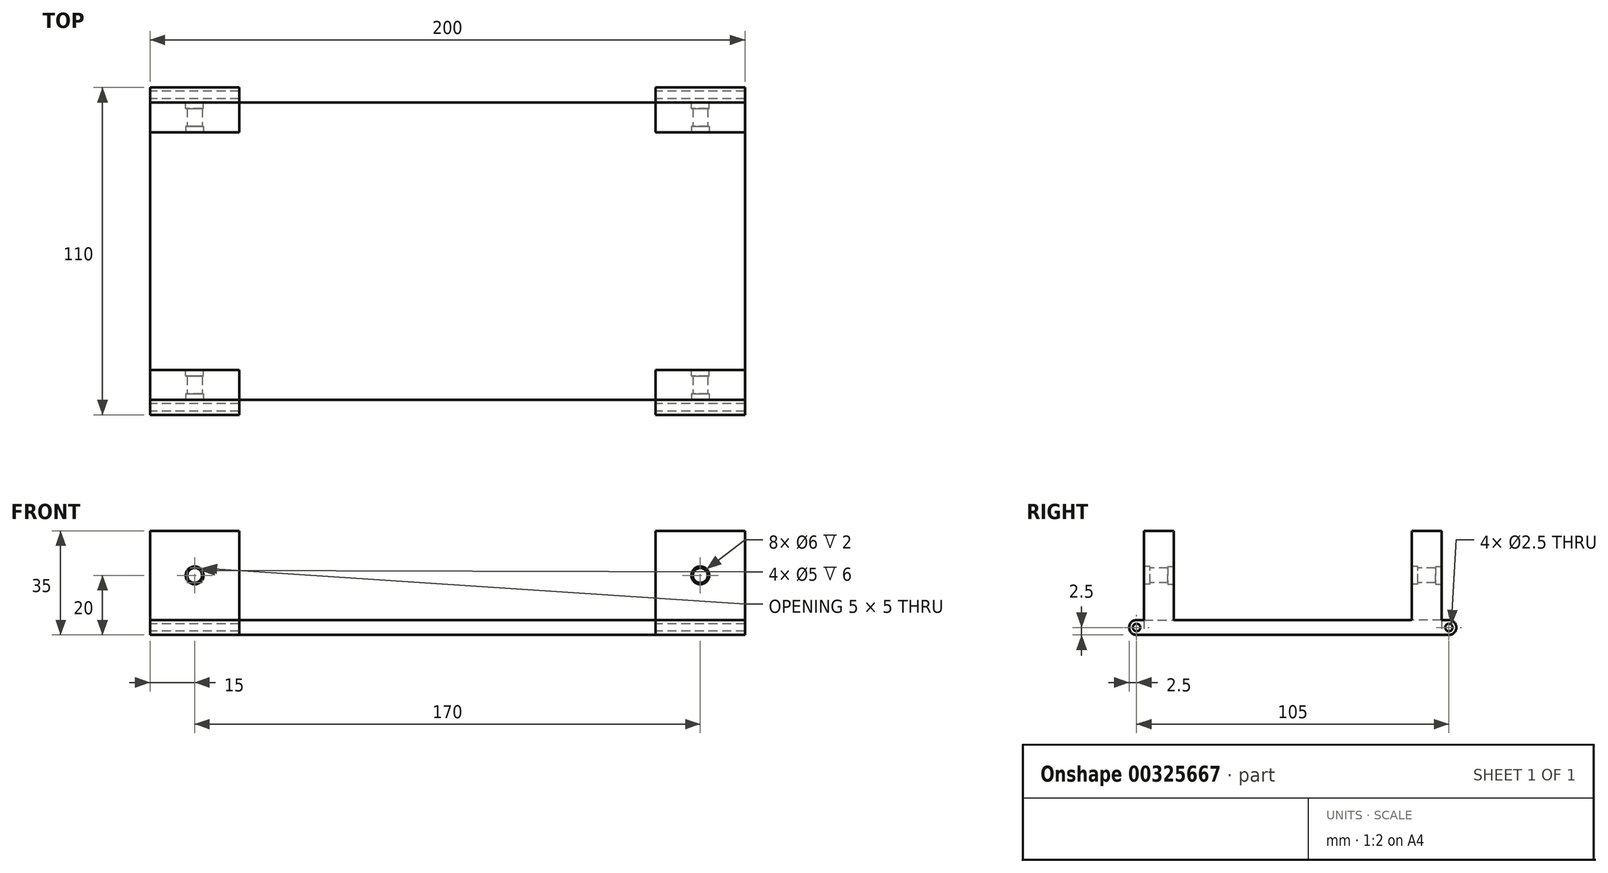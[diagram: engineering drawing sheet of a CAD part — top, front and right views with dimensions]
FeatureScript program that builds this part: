
annotation { "Feature Type Name" : "Feature", "Feature Type Description" : "" }
export const myFeature = defineFeature(function(context is Context, id is Id, definition is map)
    precondition{}
    {
        {
            var Q0;
            Q0=qCreatedBy(makeId("Top.planeOp"),FACE);
            var sketch = newSketch(context, id + "F0", { "sketchPlane" : qUnion([Q0])});
            skLineSegment(sketch, "E0.bottom", {"start": v(103.79, -50) * mm, "end": v(-96.21, -50) * mm});
            skLineSegment(sketch, "E0.top", {"start": v(103.79, 50) * mm, "end": v(-96.21, 50) * mm});
            skLineSegment(sketch, "E0.left", {"start": v(103.79, -50) * mm, "end": v(103.79, 50) * mm});
            skLineSegment(sketch, "E0.right", {"start": v(-96.21, -50) * mm, "end": v(-96.21, 50) * mm});
            skPoint(sketch, "E0.middle", {"position": v(3.79, 0) * mm});
            skSolve(sketch);
        }
        {
            var Q0;
            Q0=makeQuery(id+"F0.imprint","IMPRINT",FACE,{"disambiguationData":[TD([[makeQuery(id+"F0.imprint","IMPRINT",EDGE,{"derivedFrom":sQuery(id+"F0.wireOp",EDGE,"E0.bottom")}),-1.0]])]});
            extrude(context, id + "F1", {"entities" : qUnion([Q0]), "depth" : 5 * mm});
        }
        {
            var Q0;
            Q0=makeQuery(id+"F1.opExtrude","CAP_FACE",FACE,{"disambiguationData":[OSD([sQuery(id+"F0.wireOp",EDGE,"E0.bottom"),sQuery(id+"F0.wireOp",EDGE,"E0.top"),sQuery(id+"F0.wireOp",EDGE,"E0.left"),sQuery(id+"F0.wireOp",EDGE,"E0.right")])],"isStart":false});
            var sketch = newSketch(context, id + "F2", { "sketchPlane" : qUnion([Q0])});
            skLineSegment(sketch, "E1.bottom", {"start": v(103.79, -50) * mm, "end": v(73.79, -50) * mm});
            skLineSegment(sketch, "E1.top", {"start": v(103.79, -40) * mm, "end": v(73.79, -40) * mm});
            skLineSegment(sketch, "E1.left", {"start": v(103.79, -50) * mm, "end": v(103.79, -40) * mm});
            skLineSegment(sketch, "E1.right", {"start": v(73.79, -50) * mm, "end": v(73.79, -40) * mm});
            skLineSegment(sketch, "E2.bottom", {"start": v(103.79, 50) * mm, "end": v(73.79, 50) * mm});
            skLineSegment(sketch, "E2.top", {"start": v(103.79, 40) * mm, "end": v(73.79, 40) * mm});
            skLineSegment(sketch, "E2.left", {"start": v(103.79, 50) * mm, "end": v(103.79, 40) * mm});
            skLineSegment(sketch, "E2.right", {"start": v(73.79, 50) * mm, "end": v(73.79, 40) * mm});
            skLineSegment(sketch, "E3.bottom", {"start": v(-96.21, 50) * mm, "end": v(-66.21, 50) * mm});
            skLineSegment(sketch, "E3.top", {"start": v(-96.21, 40) * mm, "end": v(-66.21, 40) * mm});
            skLineSegment(sketch, "E3.left", {"start": v(-96.21, 50) * mm, "end": v(-96.21, 40) * mm});
            skLineSegment(sketch, "E3.right", {"start": v(-66.21, 50) * mm, "end": v(-66.21, 40) * mm});
            skLineSegment(sketch, "E4.bottom", {"start": v(-96.21, -50) * mm, "end": v(-66.21, -50) * mm});
            skLineSegment(sketch, "E4.top", {"start": v(-96.21, -40) * mm, "end": v(-66.21, -40) * mm});
            skLineSegment(sketch, "E4.left", {"start": v(-96.21, -50) * mm, "end": v(-96.21, -40) * mm});
            skLineSegment(sketch, "E4.right", {"start": v(-66.21, -50) * mm, "end": v(-66.21, -40) * mm});
            skSolve(sketch);
        }
        {
            var Q0;
            Q0=makeQuery(id+"F2.imprint","IMPRINT",FACE,{"disambiguationData":[TD([[makeQuery(id+"F2.imprint","IMPRINT",EDGE,{"derivedFrom":sQuery(id+"F2.wireOp",EDGE,"E3.bottom")}),1.0]])]});
            var Q1;
            Q1=makeQuery(id+"F2.imprint","IMPRINT",FACE,{"disambiguationData":[TD([[makeQuery(id+"F2.imprint","IMPRINT",EDGE,{"derivedFrom":sQuery(id+"F2.wireOp",EDGE,"E2.bottom")}),1.0]])]});
            var Q2;
            Q2=makeQuery(id+"F2.imprint","IMPRINT",FACE,{"disambiguationData":[TD([[makeQuery(id+"F2.imprint","IMPRINT",EDGE,{"derivedFrom":sQuery(id+"F2.wireOp",EDGE,"E4.bottom")}),-1.0]])]});
            var Q3;
            Q3=makeQuery(id+"F2.imprint","IMPRINT",FACE,{"disambiguationData":[TD([[makeQuery(id+"F2.imprint","IMPRINT",EDGE,{"derivedFrom":sQuery(id+"F2.wireOp",EDGE,"E1.bottom")}),-1.0]])]});
            extrude(context, id + "F3", {"entities" : qUnion([Q0, Q1, Q2, Q3]), "operationType" : NewBodyOperationType.ADD, "depth" : 30 * mm});
        }
        {
            var Q0;
            Q0=makeQuery(id+"F3.boolean.opBoolean","MERGE",FACE,{"derivedFrom":[makeQuery(id+"F1.opExtrude","SWEPT_FACE",FACE,{"disambiguationData":[OSD([sQuery(id+"F0.wireOp",EDGE,"E0.bottom")])]}),makeQuery(id+"F3.opExtrude","SWEPT_FACE",FACE,{"disambiguationData":[OSD([sQuery(id+"F2.wireOp",EDGE,"E1.bottom")])]}),makeQuery(id+"F3.opExtrude","SWEPT_FACE",FACE,{"disambiguationData":[OSD([sQuery(id+"F2.wireOp",EDGE,"E4.bottom")])]})]});
            var sketch = newSketch(context, id + "F4", { "sketchPlane" : qUnion([Q0])});
            skCircle(sketch, "E5", {"center": v(88.79, 20) * mm, "radius": 2.5 * mm});
            skCircle(sketch, "E6", {"center": v(-81.21, 20) * mm, "radius": 2.5 * mm});
            skSolve(sketch);
        }
        {
            var Q0;
            Q0=makeQuery(id+"F4.imprint","IMPRINT",FACE,{"disambiguationData":[TD([[makeQuery(id+"F4.imprint","IMPRINT",EDGE,{"derivedFrom":sQuery(id+"F4.wireOp",EDGE,"E5")}),1.0]])]});
            var Q1;
            Q1=makeQuery(id+"F4.imprint","IMPRINT",FACE,{"disambiguationData":[TD([[makeQuery(id+"F4.imprint","IMPRINT",EDGE,{"derivedFrom":sQuery(id+"F4.wireOp",EDGE,"E6")}),1.0]])]});
            extrude(context, id + "F5", {"entities" : qUnion([Q0, Q1]), "operationType" : NewBodyOperationType.REMOVE, "endBound" : BoundingType.THROUGH_ALL, "oppositeDirection" : true, "depth" : 25 * mm});
        }
        {
            var Q0;
            Q0=makeQuery(id+"F3.boolean.opBoolean","MERGE",FACE,{"derivedFrom":[makeQuery(id+"F1.opExtrude","SWEPT_FACE",FACE,{"disambiguationData":[OSD([sQuery(id+"F0.wireOp",EDGE,"E0.bottom")])]}),makeQuery(id+"F3.opExtrude","SWEPT_FACE",FACE,{"disambiguationData":[OSD([sQuery(id+"F2.wireOp",EDGE,"E1.bottom")])]}),makeQuery(id+"F3.opExtrude","SWEPT_FACE",FACE,{"disambiguationData":[OSD([sQuery(id+"F2.wireOp",EDGE,"E4.bottom")])]})]});
            var sketch = newSketch(context, id + "F6", { "sketchPlane" : qUnion([Q0])});
            skCircle(sketch, "E7", {"center": v(-81.21, 20) * mm, "radius": 3 * mm});
            skCircle(sketch, "E8", {"center": v(88.79, 20) * mm, "radius": 3 * mm});
            skSolve(sketch);
        }
        {
            var Q0;
            Q0=makeQuery(id+"F6.imprint","IMPRINT",FACE,{"disambiguationData":[TD([[makeQuery(id+"F6.imprint","IMPRINT",EDGE,{"derivedFrom":sQuery(id+"F6.wireOp",EDGE,"E8")}),1.0]])]});
            var Q1;
            Q1=makeQuery(id+"F6.imprint","IMPRINT",FACE,{"disambiguationData":[TD([[makeQuery(id+"F6.imprint","IMPRINT",EDGE,{"derivedFrom":sQuery(id+"F6.wireOp",EDGE,"E7")}),1.0]])]});
            extrude(context, id + "F7", {"entities" : qUnion([Q0, Q1]), "operationType" : NewBodyOperationType.REMOVE, "oppositeDirection" : true, "depth" : 2 * mm, "hasSecondDirection" : true, "secondDirectionOppositeDirection" : false, "secondDirectionDepth" : 25 * mm});
        }
        {
            var Q0;
            Q0=makeQuery(id+"F3.opExtrude","SWEPT_FACE",FACE,{"disambiguationData":[OSD([sQuery(id+"F2.wireOp",EDGE,"E3.top")])]});
            var sketch = newSketch(context, id + "F8", { "sketchPlane" : qUnion([Q0])});
            skCircle(sketch, "E9", {"center": v(-81.21, 20) * mm, "radius": 3 * mm});
            skCircle(sketch, "E10", {"center": v(88.79, 20) * mm, "radius": 3 * mm});
            skSolve(sketch);
        }
        {
            var Q0;
            Q0=makeQuery(id+"F8.imprint","IMPRINT",FACE,{"disambiguationData":[TD([[makeQuery(id+"F8.imprint","IMPRINT",EDGE,{"derivedFrom":sQuery(id+"F8.wireOp",EDGE,"E9")}),1.0]])]});
            extrude(context, id + "F9", {"entities" : qUnion([Q0]), "operationType" : NewBodyOperationType.REMOVE, "oppositeDirection" : true, "depth" : 2 * mm});
        }
        {
            var Q0;
            Q0=makeQuery(id+"F3.opExtrude","SWEPT_FACE",FACE,{"disambiguationData":[OSD([sQuery(id+"F2.wireOp",EDGE,"E2.top")])]});
            var sketch = newSketch(context, id + "F10", { "sketchPlane" : qUnion([Q0])});
            skCircle(sketch, "E11", {"center": v(88.79, 20) * mm, "radius": 3 * mm});
            skSolve(sketch);
        }
        {
            var Q0;
            Q0=makeQuery(id+"F10.imprint","IMPRINT",FACE,{"disambiguationData":[TD([[makeQuery(id+"F10.imprint","IMPRINT",EDGE,{"derivedFrom":sQuery(id+"F10.wireOp",EDGE,"E11")}),1.0]])]});
            extrude(context, id + "F11", {"entities" : qUnion([Q0]), "operationType" : NewBodyOperationType.REMOVE, "oppositeDirection" : true, "depth" : 2 * mm});
        }
        {
            var Q0;
            Q0=makeQuery(id+"F3.boolean.opBoolean","MERGE",FACE,{"derivedFrom":[makeQuery(id+"F1.opExtrude","SWEPT_FACE",FACE,{"disambiguationData":[OSD([sQuery(id+"F0.wireOp",EDGE,"E0.top")])]}),makeQuery(id+"F3.opExtrude","SWEPT_FACE",FACE,{"disambiguationData":[OSD([sQuery(id+"F2.wireOp",EDGE,"E2.bottom")])]}),makeQuery(id+"F3.opExtrude","SWEPT_FACE",FACE,{"disambiguationData":[OSD([sQuery(id+"F2.wireOp",EDGE,"E3.bottom")])]})]});
            var sketch = newSketch(context, id + "F12", { "sketchPlane" : qUnion([Q0])});
            skCircle(sketch, "E12", {"center": v(-88.79, 20) * mm, "radius": 3 * mm});
            skCircle(sketch, "E13", {"center": v(81.21, 20) * mm, "radius": 3 * mm});
            skSolve(sketch);
        }
        {
            var Q0;
            Q0=makeQuery(id+"F12.imprint","IMPRINT",FACE,{"disambiguationData":[TD([[makeQuery(id+"F12.imprint","IMPRINT",EDGE,{"derivedFrom":sQuery(id+"F12.wireOp",EDGE,"E13")}),1.0]])]});
            var Q1;
            Q1=makeQuery(id+"F12.imprint","IMPRINT",FACE,{"disambiguationData":[TD([[makeQuery(id+"F12.imprint","IMPRINT",EDGE,{"derivedFrom":sQuery(id+"F12.wireOp",EDGE,"E12")}),1.0]])]});
            extrude(context, id + "F13", {"entities" : qUnion([Q0, Q1]), "operationType" : NewBodyOperationType.REMOVE, "oppositeDirection" : true, "depth" : 2 * mm});
        }
        {
            var Q0;
            Q0=makeQuery(id+"F3.opExtrude","SWEPT_FACE",FACE,{"disambiguationData":[OSD([sQuery(id+"F2.wireOp",EDGE,"E4.top")])]});
            var sketch = newSketch(context, id + "F14", { "sketchPlane" : qUnion([Q0])});
            skCircle(sketch, "E14", {"center": v(81.21, 20) * mm, "radius": 3 * mm});
            skCircle(sketch, "E15", {"center": v(-88.79, 20) * mm, "radius": 3 * mm});
            skSolve(sketch);
        }
        {
            var Q0;
            Q0=makeQuery(id+"F14.imprint","IMPRINT",FACE,{"disambiguationData":[TD([[makeQuery(id+"F14.imprint","IMPRINT",EDGE,{"derivedFrom":makeQuery(id+"F5.boolean.opBoolean","INTERSECT",EDGE,{"derivedFrom":[makeQuery(id+"F3.opExtrude","SWEPT_FACE",FACE,{"disambiguationData":[OSD([sQuery(id+"F2.wireOp",EDGE,"E4.top")])]}),makeQuery(id+"F5.opExtrude","SWEPT_FACE",FACE,{"disambiguationData":[OSD([sQuery(id+"F4.wireOp",EDGE,"E6")])]})]})}),1.0]])]});
            var Q1;
            Q1=makeQuery(id+"F14.imprint","IMPRINT",FACE,{"disambiguationData":[TD([[makeQuery(id+"F14.imprint","IMPRINT",EDGE,{"derivedFrom":sQuery(id+"F14.wireOp",EDGE,"E14")}),1.0]])]});
            extrude(context, id + "F15", {"entities" : qUnion([Q0, Q1]), "operationType" : NewBodyOperationType.REMOVE, "oppositeDirection" : true, "depth" : 2 * mm});
        }
        {
            var Q0;
            Q0=makeQuery(id+"F3.opExtrude","SWEPT_FACE",FACE,{"disambiguationData":[OSD([sQuery(id+"F2.wireOp",EDGE,"E1.top")])]});
            var sketch = newSketch(context, id + "F16", { "sketchPlane" : qUnion([Q0])});
            skCircle(sketch, "E16", {"center": v(-88.79, 20) * mm, "radius": 3 * mm});
            skSolve(sketch);
        }
        {
            var Q0;
            Q0=makeQuery(id+"F16.imprint","IMPRINT",FACE,{"disambiguationData":[TD([[makeQuery(id+"F16.imprint","IMPRINT",EDGE,{"derivedFrom":sQuery(id+"F16.wireOp",EDGE,"E16")}),1.0]])]});
            extrude(context, id + "F17", {"entities" : qUnion([Q0]), "operationType" : NewBodyOperationType.REMOVE, "oppositeDirection" : true, "depth" : 2 * mm});
        }
        {
            var Q0;
            Q0=makeQuery(id+"F3.boolean.opBoolean","MERGE",FACE,{"derivedFrom":[makeQuery(id+"F1.opExtrude","SWEPT_FACE",FACE,{"disambiguationData":[OSD([sQuery(id+"F0.wireOp",EDGE,"E0.bottom")])]}),makeQuery(id+"F3.opExtrude","SWEPT_FACE",FACE,{"disambiguationData":[OSD([sQuery(id+"F2.wireOp",EDGE,"E1.bottom")])]}),makeQuery(id+"F3.opExtrude","SWEPT_FACE",FACE,{"disambiguationData":[OSD([sQuery(id+"F2.wireOp",EDGE,"E4.bottom")])]})]});
            var sketch = newSketch(context, id + "F18", { "sketchPlane" : qUnion([Q0])});
            skLineSegment(sketch, "E17.bottom", {"start": v(-96.21, 0) * mm, "end": v(-66.21, 0) * mm});
            skLineSegment(sketch, "E17.top", {"start": v(-96.21, 5) * mm, "end": v(-66.21, 5) * mm});
            skLineSegment(sketch, "E17.left", {"start": v(-96.21, 0) * mm, "end": v(-96.21, 5) * mm});
            skLineSegment(sketch, "E17.right", {"start": v(-66.21, 0) * mm, "end": v(-66.21, 5) * mm});
            skLineSegment(sketch, "E18.bottom", {"start": v(73.79, 5) * mm, "end": v(103.79, 5) * mm});
            skLineSegment(sketch, "E18.top", {"start": v(73.79, 0) * mm, "end": v(103.79, 0) * mm});
            skLineSegment(sketch, "E18.left", {"start": v(73.79, 5) * mm, "end": v(73.79, 0) * mm});
            skLineSegment(sketch, "E18.right", {"start": v(103.79, 5) * mm, "end": v(103.79, 0) * mm});
            skSolve(sketch);
        }
        {
            var Q0;
            Q0=makeQuery(id+"F18.imprint","IMPRINT",FACE,{"disambiguationData":[TD([[makeQuery(id+"F18.imprint","IMPRINT",EDGE,{"derivedFrom":sQuery(id+"F18.wireOp",EDGE,"E17.bottom")}),-1.0]])]});
            var Q1;
            Q1=makeQuery(id+"F18.imprint","IMPRINT",FACE,{"disambiguationData":[TD([[makeQuery(id+"F18.imprint","IMPRINT",EDGE,{"derivedFrom":sQuery(id+"F18.wireOp",EDGE,"E18.bottom")}),-1.0]])]});
            extrude(context, id + "F19", {"entities" : qUnion([Q0, Q1]), "operationType" : NewBodyOperationType.ADD, "depth" : 5 * mm});
        }
        {
            var Q0;
            Q0=makeQuery(id+"F19.boolean.opBoolean","MERGE",FACE,{"derivedFrom":[makeQuery(id+"F3.boolean.opBoolean","MERGE",FACE,{"derivedFrom":[makeQuery(id+"F1.opExtrude","SWEPT_FACE",FACE,{"disambiguationData":[OSD([sQuery(id+"F0.wireOp",EDGE,"E0.right")])]}),makeQuery(id+"F3.opExtrude","SWEPT_FACE",FACE,{"disambiguationData":[OSD([sQuery(id+"F2.wireOp",EDGE,"E3.left")])]}),makeQuery(id+"F3.opExtrude","SWEPT_FACE",FACE,{"disambiguationData":[OSD([sQuery(id+"F2.wireOp",EDGE,"E4.left")])]})]}),makeQuery(id+"F19.opExtrude","SWEPT_FACE",FACE,{"disambiguationData":[OSD([sQuery(id+"F18.wireOp",EDGE,"E17.left")])]})]});
            var sketch = newSketch(context, id + "F20", { "sketchPlane" : qUnion([Q0])});
            skCircle(sketch, "E19", {"center": v(52.5, 2.5) * mm, "radius": 1.25 * mm});
            skSolve(sketch);
        }
        {
            var Q0;
            Q0=makeQuery(id+"F20.imprint","IMPRINT",FACE,{"disambiguationData":[TD([[makeQuery(id+"F20.imprint","IMPRINT",EDGE,{"derivedFrom":sQuery(id+"F20.wireOp",EDGE,"E19")}),1.0]])]});
            extrude(context, id + "F21", {"entities" : qUnion([Q0]), "operationType" : NewBodyOperationType.REMOVE, "endBound" : BoundingType.THROUGH_ALL, "oppositeDirection" : true, "depth" : 25 * mm});
        }
        {
            var Q0;
            Q0=makeQuery(id+"F19.opExtrude","CAP_EDGE",EDGE,{"disambiguationData":[OSD([sQuery(id+"F18.wireOp",EDGE,"E17.top")])],"isStart":false});
            var Q1;
            Q1=makeQuery(id+"F19.opExtrude","CAP_EDGE",EDGE,{"disambiguationData":[OSD([sQuery(id+"F18.wireOp",EDGE,"E17.bottom")])],"isStart":false});
            var Q2;
            Q2=makeQuery(id+"F19.opExtrude","CAP_EDGE",EDGE,{"disambiguationData":[OSD([sQuery(id+"F18.wireOp",EDGE,"E18.bottom")])],"isStart":false});
            var Q3;
            Q3=makeQuery(id+"F19.opExtrude","CAP_EDGE",EDGE,{"disambiguationData":[OSD([sQuery(id+"F18.wireOp",EDGE,"E18.top")])],"isStart":false});
            fillet(context, id + "F22", {"entities" : qUnion([Q0, Q1, Q2, Q3]), "radius" : 2.5 * mm, "tangentPropagation" : true, "allowEdgeOverflow" : false});
        }
        {
            var Q0;
            Q0=makeQuery(id+"F3.boolean.opBoolean","MERGE",FACE,{"derivedFrom":[makeQuery(id+"F1.opExtrude","SWEPT_FACE",FACE,{"disambiguationData":[OSD([sQuery(id+"F0.wireOp",EDGE,"E0.top")])]}),makeQuery(id+"F3.opExtrude","SWEPT_FACE",FACE,{"disambiguationData":[OSD([sQuery(id+"F2.wireOp",EDGE,"E2.bottom")])]}),makeQuery(id+"F3.opExtrude","SWEPT_FACE",FACE,{"disambiguationData":[OSD([sQuery(id+"F2.wireOp",EDGE,"E3.bottom")])]})]});
            var sketch = newSketch(context, id + "F23", { "sketchPlane" : qUnion([Q0])});
            skLineSegment(sketch, "E20.bottom", {"start": v(66.21, 5) * mm, "end": v(96.21, 5) * mm});
            skLineSegment(sketch, "E20.top", {"start": v(66.21, 0) * mm, "end": v(96.21, 0) * mm});
            skLineSegment(sketch, "E20.left", {"start": v(66.21, 5) * mm, "end": v(66.21, 0) * mm});
            skLineSegment(sketch, "E20.right", {"start": v(96.21, 5) * mm, "end": v(96.21, 0) * mm});
            skLineSegment(sketch, "E21.bottom", {"start": v(-73.79, 5) * mm, "end": v(-103.79, 5) * mm});
            skLineSegment(sketch, "E21.top", {"start": v(-73.79, 0) * mm, "end": v(-103.79, 0) * mm});
            skLineSegment(sketch, "E21.left", {"start": v(-73.79, 5) * mm, "end": v(-73.79, 0) * mm});
            skLineSegment(sketch, "E21.right", {"start": v(-103.79, 5) * mm, "end": v(-103.79, 0) * mm});
            skSolve(sketch);
        }
        {
            var Q0;
            Q0=makeQuery(id+"F23.imprint","IMPRINT",FACE,{"disambiguationData":[TD([[makeQuery(id+"F23.imprint","IMPRINT",EDGE,{"derivedFrom":sQuery(id+"F23.wireOp",EDGE,"E21.bottom")}),1.0]])]});
            var Q1;
            Q1=makeQuery(id+"F23.imprint","IMPRINT",FACE,{"disambiguationData":[TD([[makeQuery(id+"F23.imprint","IMPRINT",EDGE,{"derivedFrom":sQuery(id+"F23.wireOp",EDGE,"E20.bottom")}),-1.0]])]});
            extrude(context, id + "F24", {"entities" : qUnion([Q0, Q1]), "operationType" : NewBodyOperationType.ADD, "depth" : 5 * mm});
        }
        {
            var Q0;
            Q0=makeQuery(id+"F24.boolean.opBoolean","MERGE",FACE,{"derivedFrom":[makeQuery(id+"F19.boolean.opBoolean","MERGE",FACE,{"derivedFrom":[makeQuery(id+"F3.boolean.opBoolean","MERGE",FACE,{"derivedFrom":[makeQuery(id+"F1.opExtrude","SWEPT_FACE",FACE,{"disambiguationData":[OSD([sQuery(id+"F0.wireOp",EDGE,"E0.right")])]}),makeQuery(id+"F3.opExtrude","SWEPT_FACE",FACE,{"disambiguationData":[OSD([sQuery(id+"F2.wireOp",EDGE,"E3.left")])]}),makeQuery(id+"F3.opExtrude","SWEPT_FACE",FACE,{"disambiguationData":[OSD([sQuery(id+"F2.wireOp",EDGE,"E4.left")])]})]}),makeQuery(id+"F19.opExtrude","SWEPT_FACE",FACE,{"disambiguationData":[OSD([sQuery(id+"F18.wireOp",EDGE,"E17.left")])]})]}),makeQuery(id+"F24.opExtrude","SWEPT_FACE",FACE,{"disambiguationData":[OSD([sQuery(id+"F23.wireOp",EDGE,"E20.right")])]})]});
            var sketch = newSketch(context, id + "F25", { "sketchPlane" : qUnion([Q0])});
            skCircle(sketch, "E22", {"center": v(-52.5, 2.5) * mm, "radius": 1.25 * mm});
            skPoint(sketch, "E22.centerSnap0", {"position": v(-52.5, 5) * mm});
            skSolve(sketch);
        }
        {
            var Q0;
            Q0=makeQuery(id+"F25.imprint","IMPRINT",FACE,{"disambiguationData":[TD([[makeQuery(id+"F25.imprint","IMPRINT",EDGE,{"derivedFrom":sQuery(id+"F25.wireOp",EDGE,"E22")}),1.0]])]});
            extrude(context, id + "F26", {"entities" : qUnion([Q0]), "operationType" : NewBodyOperationType.REMOVE, "endBound" : BoundingType.THROUGH_ALL, "oppositeDirection" : true, "depth" : 25 * mm});
        }
        {
            var Q0;
            Q0=makeQuery(id+"F24.opExtrude","CAP_EDGE",EDGE,{"disambiguationData":[OSD([sQuery(id+"F23.wireOp",EDGE,"E21.bottom")])],"isStart":false});
            var Q1;
            Q1=makeQuery(id+"F24.opExtrude","CAP_EDGE",EDGE,{"disambiguationData":[OSD([sQuery(id+"F23.wireOp",EDGE,"E21.top")])],"isStart":false});
            var Q2;
            Q2=makeQuery(id+"F24.opExtrude","CAP_EDGE",EDGE,{"disambiguationData":[OSD([sQuery(id+"F23.wireOp",EDGE,"E20.top")])],"isStart":false});
            var Q3;
            Q3=makeQuery(id+"F24.opExtrude","CAP_EDGE",EDGE,{"disambiguationData":[OSD([sQuery(id+"F23.wireOp",EDGE,"E20.bottom")])],"isStart":false});
            fillet(context, id + "F27", {"entities" : qUnion([Q0, Q1, Q2, Q3]), "radius" : 2.5 * mm, "tangentPropagation" : true, "allowEdgeOverflow" : false});
        }
    });
